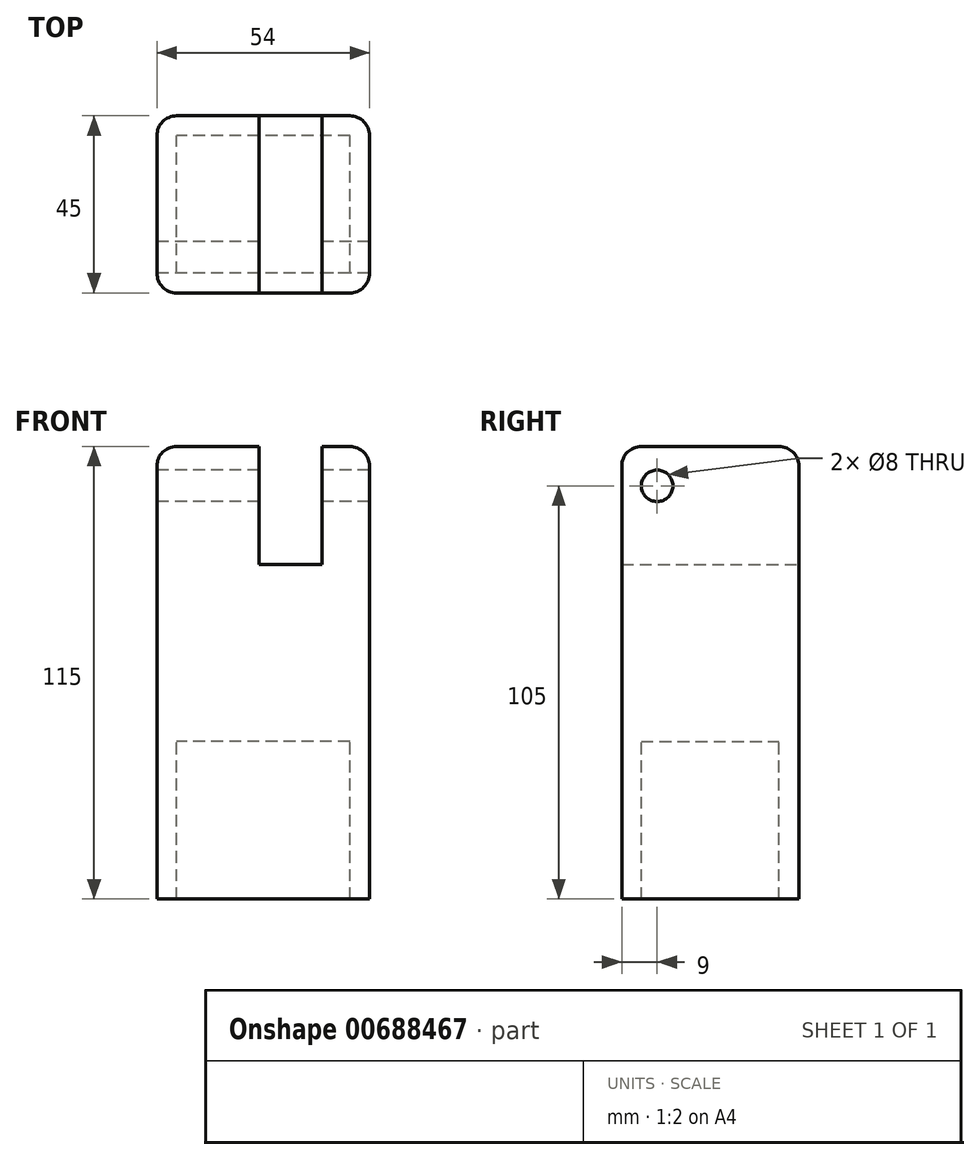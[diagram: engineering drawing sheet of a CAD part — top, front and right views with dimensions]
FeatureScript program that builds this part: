
annotation { "Feature Type Name" : "Feature", "Feature Type Description" : "" }
export const myFeature = defineFeature(function(context is Context, id is Id, definition is map)
    precondition{}
    {
        {
            var Q0;
            Q0=qCreatedBy(makeId("Top.planeOp"),FACE);
            var sketch = newSketch(context, id + "F0", { "sketchPlane" : qUnion([Q0])});
            skLineSegment(sketch, "E0.bottom", {"start": v(22, -17.5) * mm, "end": v(-22, -17.5) * mm});
            skLineSegment(sketch, "E0.top", {"start": v(22, 17.5) * mm, "end": v(-22, 17.5) * mm});
            skLineSegment(sketch, "E0.left", {"start": v(22, -17.5) * mm, "end": v(22, 17.5) * mm});
            skLineSegment(sketch, "E0.right", {"start": v(-22, -17.5) * mm, "end": v(-22, 17.5) * mm});
            skPoint(sketch, "E0.middle", {"position": v(0, 0) * mm});
            skLineSegment(sketch, "E1.0", {"start": v(27, -22.5) * mm, "end": v(-27, -22.5) * mm});
            skLineSegment(sketch, "E1.1", {"start": v(27, -22.5) * mm, "end": v(27, 22.5) * mm});
            skLineSegment(sketch, "E1.2", {"start": v(27, 22.5) * mm, "end": v(-27, 22.5) * mm});
            skLineSegment(sketch, "E1.3", {"start": v(-27, -22.5) * mm, "end": v(-27, 22.5) * mm});
            skSolve(sketch);
        }
        {
            var Q0;
            Q0 = qSketchRegion(id + "F0", true);
            extrude(context, id + "F1", {"entities" : qUnion([Q0]), "oppositeDirection" : true, "depth" : 40 * mm, "offsetDistance" : 25 * mm});
        }
        {
            var Q0;
            Q0=makeQuery(id+"F0.imprint","IMPRINT",FACE,{"disambiguationData":[TD([[makeQuery(id+"F0.imprint","IMPRINT",EDGE,{"derivedFrom":sQuery(id+"F0.wireOp",EDGE,"E0.bottom")}),1.0]])]});
            var Q1;
            Q1=makeQuery(id+"F0.imprint","IMPRINT",FACE,{"disambiguationData":[TD([[makeQuery(id+"F0.imprint","IMPRINT",EDGE,{"derivedFrom":sQuery(id+"F0.wireOp",EDGE,"E0.bottom")}),-1.0]])]});
            extrude(context, id + "F2", {"entities" : qUnion([Q0, Q1]), "operationType" : NewBodyOperationType.ADD, "depth" : 5 * mm, "offsetDistance" : 25 * mm});
        }
        {
            var Q0;
            Q0=makeQuery(id+"F2.opExtrude","CAP_FACE",FACE,{"disambiguationData":[OSD([sQuery(id+"F0.wireOp",EDGE,"E1.0"),sQuery(id+"F0.wireOp",EDGE,"E1.1"),sQuery(id+"F0.wireOp",EDGE,"E1.2"),sQuery(id+"F0.wireOp",EDGE,"E1.3")])],"isStart":false});
            var sketch = newSketch(context, id + "F3", { "sketchPlane" : qUnion([Q0])});
            skLineSegment(sketch, "E2.bottom", {"start": v(27, -22.5) * mm, "end": v(21, -22.5) * mm});
            skLineSegment(sketch, "E2.top", {"start": v(27, 22.5) * mm, "end": v(21, 22.5) * mm});
            skLineSegment(sketch, "E2.left", {"start": v(27, -22.5) * mm, "end": v(27, 22.5) * mm});
            skLineSegment(sketch, "E2.right", {"start": v(21, -22.5) * mm, "end": v(21, 22.5) * mm});
            skLineSegment(sketch, "E3.bottom", {"start": v(-27, 22.5) * mm, "end": v(-21, 22.5) * mm});
            skLineSegment(sketch, "E3.top", {"start": v(-27, -22.5) * mm, "end": v(-21, -22.5) * mm});
            skLineSegment(sketch, "E3.left", {"start": v(-27, 22.5) * mm, "end": v(-27, -22.5) * mm});
            skLineSegment(sketch, "E3.right", {"start": v(-21, 22.5) * mm, "end": v(-21, -22.5) * mm});
            skSolve(sketch);
        }
        {
            var Q0;
            Q0 = qSketchRegion(id + "F3", true);
            extrude(context, id + "F4", {"entities" : qUnion([Q0]), "operationType" : NewBodyOperationType.ADD, "depth" : 70 * mm, "offsetDistance" : 25 * mm});
        }
        {
            var Q0;
            Q0=makeQuery(id+"F4.opExtrude","SWEPT_FACE",FACE,{"disambiguationData":[OSD([sQuery(id+"F3.wireOp",EDGE,"E3.right")])]});
            var sketch = newSketch(context, id + "F5", { "sketchPlane" : qUnion([Q0])});
            skCircle(sketch, "E4", {"center": v(-13.5, 65) * mm, "radius": 4 * mm});
            skSolve(sketch);
        }
        {
            var Q0;
            Q0=makeQuery(id+"F4.opExtrude","CAP_EDGE",EDGE,{"disambiguationData":[OSD([sQuery(id+"F3.wireOp",EDGE,"E3.top")])],"isStart":false});
            var Q1;
            Q1=makeQuery(id+"F4.opExtrude","CAP_EDGE",EDGE,{"disambiguationData":[OSD([sQuery(id+"F3.wireOp",EDGE,"E3.bottom")])],"isStart":false});
            var Q2;
            Q2=makeQuery(id+"F4.opExtrude","CAP_EDGE",EDGE,{"disambiguationData":[OSD([sQuery(id+"F3.wireOp",EDGE,"E2.bottom")])],"isStart":false});
            var Q3;
            Q3=makeQuery(id+"F4.opExtrude","CAP_EDGE",EDGE,{"disambiguationData":[OSD([sQuery(id+"F3.wireOp",EDGE,"E2.top")])],"isStart":false});
            var Q4;
            {var subQ0=sQuery(id+"F0.wireOp",EDGE,"E1.1");var subQ1=sQuery(id+"F0.wireOp",EDGE,"E1.0");Q4=makeQuery(id+"F4.boolean.opBoolean","MERGE",EDGE,{"derivedFrom":[makeQuery(id+"F2.boolean.opBoolean","MERGE",EDGE,{"derivedFrom":[makeQuery(id+"F1.opExtrude","SWEPT_EDGE",EDGE,{"disambiguationData":[OSD([subQ1,subQ0])]}),makeQuery(id+"F2.opExtrude","SWEPT_EDGE",EDGE,{"disambiguationData":[OSD([subQ1,subQ0])]})]}),makeQuery(id+"F4.opExtrude","SWEPT_EDGE",EDGE,{"disambiguationData":[OSD([sQuery(id+"F3.wireOp",EDGE,"E2.bottom"),sQuery(id+"F3.wireOp",EDGE,"E2.left")])]})]});}
            var Q5;
            Q5=makeQuery(id+"F4.opExtrude","CAP_EDGE",EDGE,{"disambiguationData":[OSD([sQuery(id+"F3.wireOp",EDGE,"E2.left")])],"isStart":false});
            var Q6;
            {var subQ0=sQuery(id+"F0.wireOp",EDGE,"E1.2");var subQ1=sQuery(id+"F0.wireOp",EDGE,"E1.1");Q6=makeQuery(id+"F4.boolean.opBoolean","MERGE",EDGE,{"derivedFrom":[makeQuery(id+"F2.boolean.opBoolean","MERGE",EDGE,{"derivedFrom":[makeQuery(id+"F1.opExtrude","SWEPT_EDGE",EDGE,{"disambiguationData":[OSD([subQ1,subQ0])]}),makeQuery(id+"F2.opExtrude","SWEPT_EDGE",EDGE,{"disambiguationData":[OSD([subQ1,subQ0])]})]}),makeQuery(id+"F4.opExtrude","SWEPT_EDGE",EDGE,{"disambiguationData":[OSD([sQuery(id+"F3.wireOp",EDGE,"E2.top"),sQuery(id+"F3.wireOp",EDGE,"E2.left")])]})]});}
            var Q7;
            {var subQ0=sQuery(id+"F0.wireOp",EDGE,"E1.3");var subQ1=sQuery(id+"F0.wireOp",EDGE,"E1.0");Q7=makeQuery(id+"F4.boolean.opBoolean","MERGE",EDGE,{"derivedFrom":[makeQuery(id+"F2.boolean.opBoolean","MERGE",EDGE,{"derivedFrom":[makeQuery(id+"F1.opExtrude","SWEPT_EDGE",EDGE,{"disambiguationData":[OSD([subQ1,subQ0])]}),makeQuery(id+"F2.opExtrude","SWEPT_EDGE",EDGE,{"disambiguationData":[OSD([subQ1,subQ0])]})]}),makeQuery(id+"F4.opExtrude","SWEPT_EDGE",EDGE,{"disambiguationData":[OSD([sQuery(id+"F3.wireOp",EDGE,"E3.top"),sQuery(id+"F3.wireOp",EDGE,"E3.left")])]})]});}
            var Q8;
            {var subQ0=sQuery(id+"F0.wireOp",EDGE,"E1.3");var subQ1=sQuery(id+"F0.wireOp",EDGE,"E1.2");Q8=makeQuery(id+"F4.boolean.opBoolean","MERGE",EDGE,{"derivedFrom":[makeQuery(id+"F2.boolean.opBoolean","MERGE",EDGE,{"derivedFrom":[makeQuery(id+"F1.opExtrude","SWEPT_EDGE",EDGE,{"disambiguationData":[OSD([subQ1,subQ0])]}),makeQuery(id+"F2.opExtrude","SWEPT_EDGE",EDGE,{"disambiguationData":[OSD([subQ1,subQ0])]})]}),makeQuery(id+"F4.opExtrude","SWEPT_EDGE",EDGE,{"disambiguationData":[OSD([sQuery(id+"F3.wireOp",EDGE,"E3.bottom"),sQuery(id+"F3.wireOp",EDGE,"E3.left")])]})]});}
            var Q9;
            Q9=makeQuery(id+"F4.opExtrude","CAP_EDGE",EDGE,{"disambiguationData":[OSD([sQuery(id+"F3.wireOp",EDGE,"E3.left")])],"isStart":false});
            fillet(context, id + "F6", {"entities" : qUnion([Q0, Q1, Q2, Q3, Q4, Q5, Q6, Q7, Q8, Q9]), "radius" : 5 * mm, "tangentPropagation" : true, "allowEdgeOverflow" : false});
        }
        {
            var Q0;
            Q0=makeQuery(id+"F2.opExtrude","CAP_FACE",FACE,{"disambiguationData":[OSD([sQuery(id+"F0.wireOp",EDGE,"E1.0"),sQuery(id+"F0.wireOp",EDGE,"E1.1"),sQuery(id+"F0.wireOp",EDGE,"E1.2"),sQuery(id+"F0.wireOp",EDGE,"E1.3")])],"isStart":false});
            extrude(context, id + "F7", {"entities" : qUnion([Q0]), "operationType" : NewBodyOperationType.ADD, "depth" : 40 * mm, "offsetDistance" : 25 * mm});
        }
        {
            var Q0;
            Q0=makeQuery(id+"F5.imprint","IMPRINT",FACE,{"disambiguationData":[TD([[makeQuery(id+"F5.imprint","IMPRINT",EDGE,{"derivedFrom":sQuery(id+"F5.wireOp",EDGE,"E4")}),1.0]])]});
            extrude(context, id + "F8", {"entities" : qUnion([Q0]), "operationType" : NewBodyOperationType.REMOVE, "endBound" : BoundingType.THROUGH_ALL, "depth" : 25 * mm, "offsetDistance" : 25 * mm, "hasSecondDirection" : true, "secondDirectionOppositeDirection" : true, "secondDirectionDepth" : 25 * mm});
        }
        {
            var Q0;
            Q0=makeQuery(id+"F4.opExtrude","SWEPT_FACE",FACE,{"disambiguationData":[OSD([sQuery(id+"F3.wireOp",EDGE,"E3.right")])]});
            extrude(context, id + "F9", {"entities" : qUnion([Q0]), "operationType" : NewBodyOperationType.ADD, "depth" : 20 * mm, "offsetDistance" : 25 * mm});
        }
        {
            var Q0;
            Q0=makeQuery(id+"F4.opExtrude","SWEPT_FACE",FACE,{"disambiguationData":[OSD([sQuery(id+"F3.wireOp",EDGE,"E2.right")])]});
            extrude(context, id + "F10", {"entities" : qUnion([Q0]), "operationType" : NewBodyOperationType.ADD, "depth" : 6 * mm, "offsetDistance" : 25 * mm});
        }
    });
